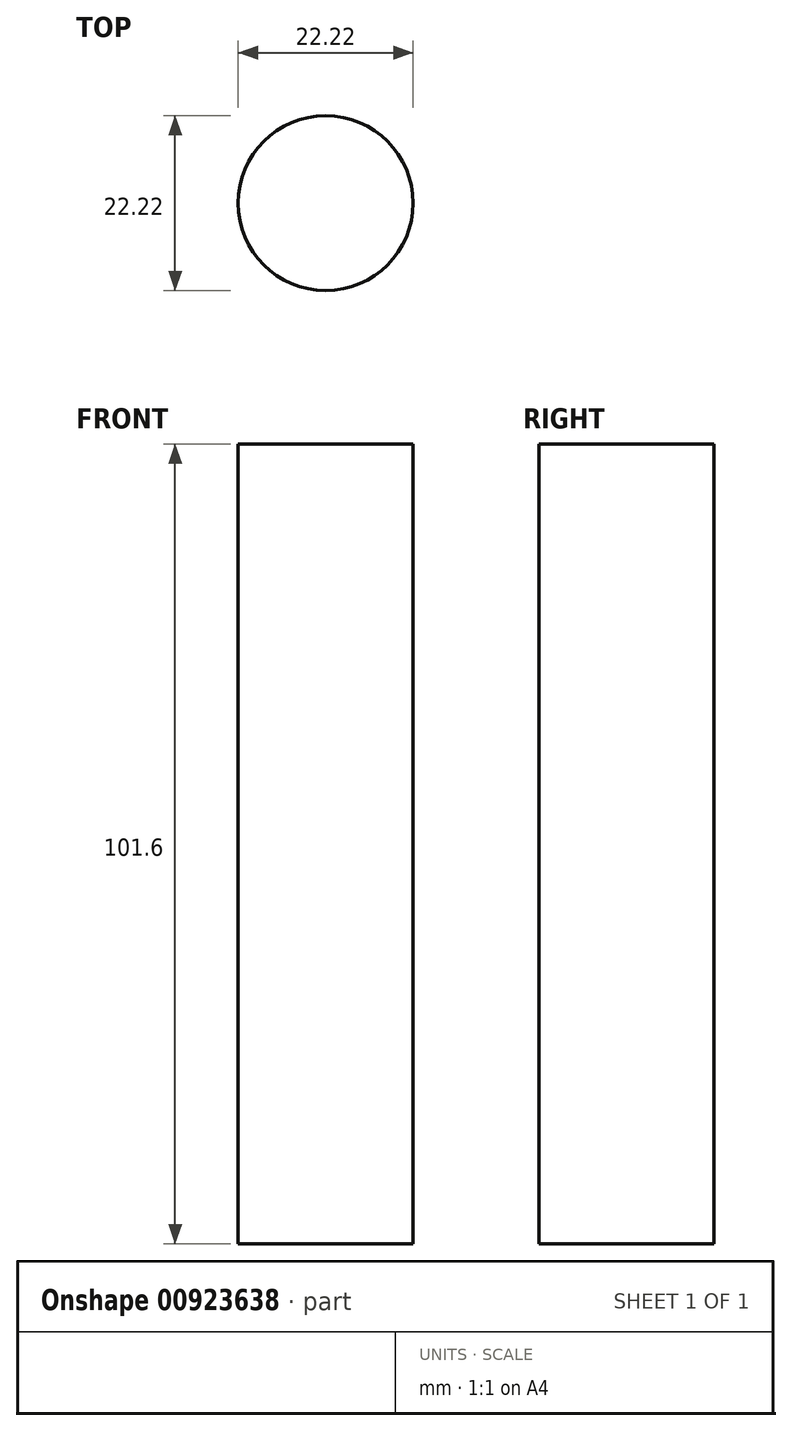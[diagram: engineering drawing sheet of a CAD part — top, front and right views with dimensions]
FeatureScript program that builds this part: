
annotation { "Feature Type Name" : "Feature", "Feature Type Description" : "" }
export const myFeature = defineFeature(function(context is Context, id is Id, definition is map)
    precondition{}
    {
        {
            var Q0;
            Q0=qCreatedBy(makeId("Top.planeOp"),FACE);
            var sketch = newSketch(context, id + "F0", { "sketchPlane" : qUnion([Q0])});
            skCircle(sketch, "E0", {"center": v(0, 0) * mm, "radius": 11.11 * mm});
            skSolve(sketch);
        }
        {
            var Q0;
            Q0=qSketchRegion(id+"F0",true);
            extrude(context, id + "F1", {"entities" : qUnion([Q0]), "depth" : 101.6 * mm});
        }
    });
